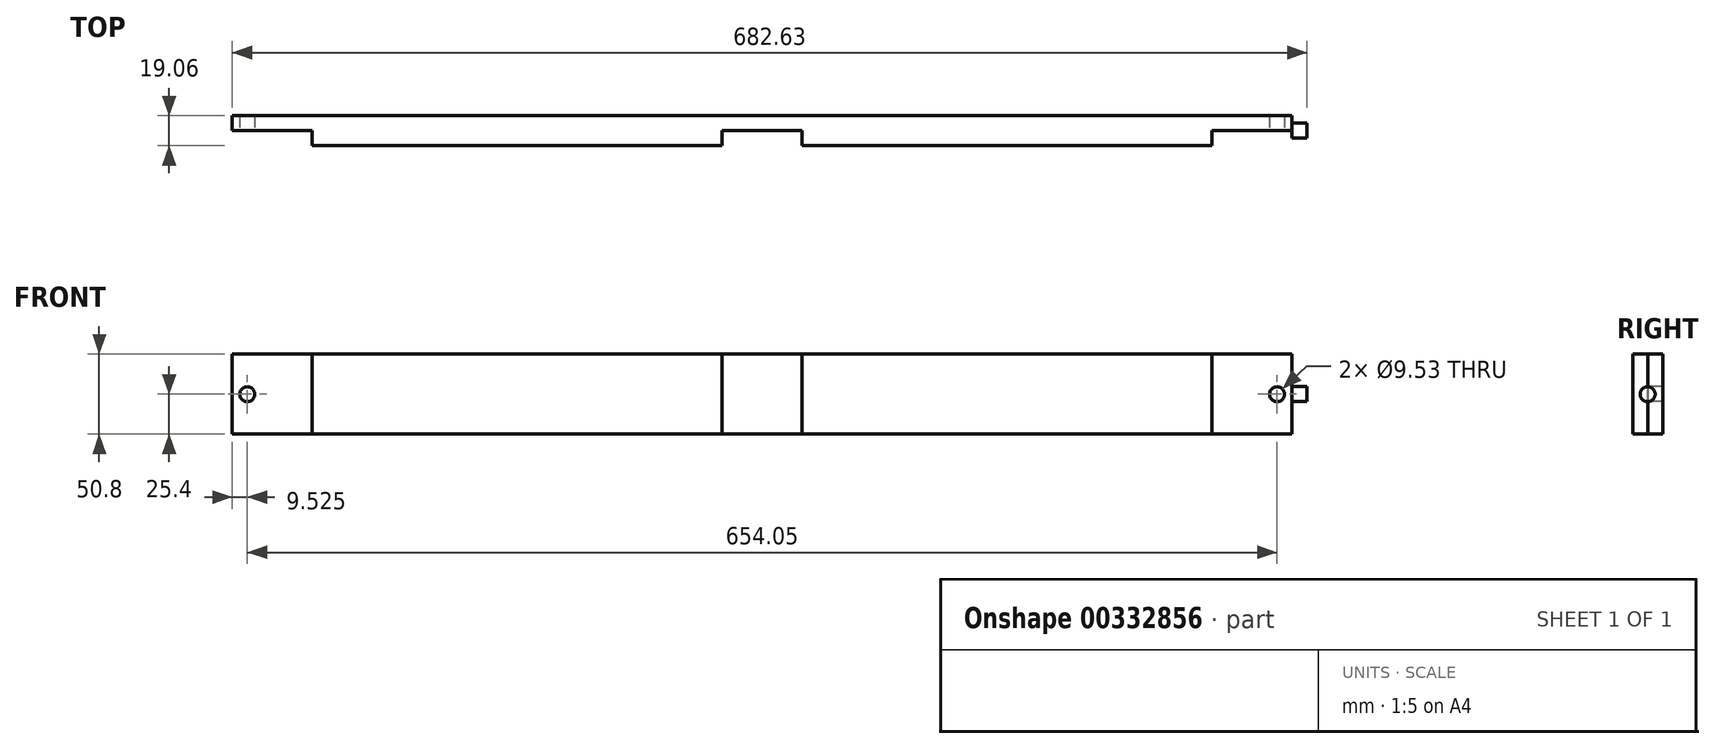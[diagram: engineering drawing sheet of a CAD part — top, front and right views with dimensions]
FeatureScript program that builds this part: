
annotation { "Feature Type Name" : "Feature", "Feature Type Description" : "" }
export const myFeature = defineFeature(function(context is Context, id is Id, definition is map)
    precondition{}
    {
        {
            var Q0;
            Q0=qCreatedBy(makeId("Top.planeOp"),FACE);
            var sketch = newSketch(context, id + "F0", { "sketchPlane" : qUnion([Q0])});
            skLineSegment(sketch, "E0.bottom", {"start": v(-622.3, -9.53) * mm, "end": v(-521.56, -9.53) * mm});
            skLineSegment(sketch, "E0.right", {"start": v(0, 0) * mm, "end": v(0, 9.52) * mm});
            skLineSegment(sketch, "E1", {"start": v(0, 9.52) * mm, "end": v(-673.1, 9.52) * mm});
            skPoint(sketch, "E2.left.start.orphan", {"position": v(-777.73, -5.46) * mm});
            skLineSegment(sketch, "E3.trimOffspring", {"start": v(-521.56, -9.53) * mm, "end": v(-470.76, -9.53) * mm});
            skLineSegment(sketch, "E4.top", {"start": v(-673.1, 0) * mm, "end": v(-622.3, 0) * mm});
            skLineSegment(sketch, "E4.left", {"start": v(-673.1, 0) * mm, "end": v(-673.1, 9.52) * mm});
            skLineSegment(sketch, "E4.right", {"start": v(-622.3, -9.53) * mm, "end": v(-622.3, 0) * mm});
            skLineSegment(sketch, "E5.trimOffspring", {"start": v(-622.3, -9.53) * mm, "end": v(-361.95, -9.53) * mm});
            skLineSegment(sketch, "E6.top", {"start": v(-50.8, 0) * mm, "end": v(0, 0) * mm});
            skLineSegment(sketch, "E6.left", {"start": v(-50.8, -9.53) * mm, "end": v(-50.8, 0) * mm});
            skPoint(sketch, "E7.orphan", {"position": v(0, -9.53) * mm});
            skLineSegment(sketch, "E8.bottom", {"start": v(-311.15, 0) * mm, "end": v(-361.95, 0) * mm});
            skLineSegment(sketch, "E8.left", {"start": v(-311.15, 0) * mm, "end": v(-311.15, -9.53) * mm});
            skLineSegment(sketch, "E8.right", {"start": v(-361.95, 0) * mm, "end": v(-361.95, -9.53) * mm});
            skPoint(sketch, "E8.middle", {"position": v(-336.55, -9.53) * mm});
            skPoint(sketch, "E9.orphan", {"position": v(-361.95, -19.05) * mm});
            skLineSegment(sketch, "E10.trimOffspring", {"start": v(-311.15, -9.53) * mm, "end": v(-50.8, -9.53) * mm});
            skPoint(sketch, "E11.orphan", {"position": v(-311.15, -19.05) * mm});
            skSolve(sketch);
        }
        {
            var Q0;
            Q0=qSketchRegion(id+"F0",true);
            extrude(context, id + "F1", {"entities" : qUnion([Q0]), "endBound" : BoundingType.SYMMETRIC, "depth" : 50.8 * mm});
        }
        {
            var Q0;
            Q0=qCreatedBy(makeId("Right.planeOp"),FACE);
            var sketch = newSketch(context, id + "F2", { "sketchPlane" : qUnion([Q0])});
            skCircle(sketch, "E12", {"center": v(0, 0) * mm, "radius": 4.76 * mm});
            skSolve(sketch);
        }
        {
            var Q0;
            Q0=qSketchRegion(id+"F2",true);
            extrude(context, id + "F3", {"entities" : qUnion([Q0]), "operationType" : NewBodyOperationType.ADD, "depth" : 9.52 * mm});
        }
        {
            var Q0;
            Q0=qCreatedBy(makeId("Front.planeOp"),FACE);
            var sketch = newSketch(context, id + "F4", { "sketchPlane" : qUnion([Q0])});
            skCircle(sketch, "E13", {"center": v(-663.57, 0) * mm, "radius": 4.76 * mm});
            skCircle(sketch, "E14", {"center": v(-9.52, 0) * mm, "radius": 4.76 * mm});
            skSolve(sketch);
        }
        {
            var Q0;
            Q0=qSketchRegion(id+"F4",true);
            extrude(context, id + "F5", {"entities" : qUnion([Q0]), "operationType" : NewBodyOperationType.REMOVE, "oppositeDirection" : true, "depth" : 25.4 * mm});
        }
    });
